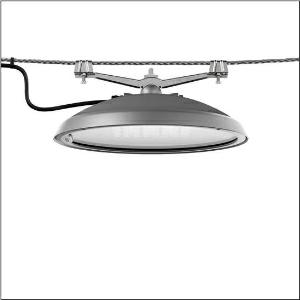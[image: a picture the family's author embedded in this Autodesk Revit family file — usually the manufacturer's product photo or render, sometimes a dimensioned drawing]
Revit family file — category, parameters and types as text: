
# Revit family: dl_50_iq_mini___p1_0s_5xa248u31f08ge_bd95
name_source: partatom
category: Lighting Fixtures
units: mm (PartAtom-declared; Revit-internal decimal feet)

## family parameters
Cut with Voids When Loaded = No
Host = Face
Light Source = No
Part Type = Normal
Room Calculation Point = No
Round Connector Dimension = Use Diameter
Shared = No

## types (1)
- --- (1 x LED, 5030 lm, 32.7 W, 3000K)
    Apparent Load = 33 VA
    CIE Flux Codes = 23 54 93 100 100
    Color Rendering = 70
    Color Temperature = 3000K
    Default Elevation = 1800 mm
    Description = DL 50 iQ mini, catenary luminaire, primary light control with lens, of PMMA, primary optical cover: cover, of toughened safety glass, transparent, light distribution: P1.0s, light emission: direct distribution, primary light characteristic: symmetric, installation type: suspended mounting, LED, High Power LED, rated luminous flux: 5.030lm, luminous efficacy: 154lm/W, light colour: 730, colour temperature: 3000K, control gear: iQ Street-Remote, control: optimised constant luminous flux control (CLO 2.0), Desk-Remote (wireless, voltage-free reading and setting of iQ features in the workshop via application-optimized NFC function/RFID function), Light-Fading, Smart-Wire, Night-Set, Lumen-Switch, Temp-Guard, Auto-Match, Street-Remote, mains connection: 230..240V, AC, 50/60Hz, start of lifetime: 33W, end of service life: 34W, reduction: 16W, luminaire housing, of diecast aluminium, powder-coated, SITECO metallic grey (DB 702S), diameter: 500mm, height: 115mm, mounting height: 4..12m, protection rating (complete): IP66, insulation class (complete): insulation class II (safety insulation), certification: CE, ENEC, ENEC+, VDE, impact resistance: IK08, permissible operating ambient temperature for outdoor applications: -25..+40°C, standard-compliant lighting for roads and squares, packaging unit: 1 piece

Light Distribution: P1.0s
    Height = 124 mm
    Lamp = 1 x LED
    Lamp Light Flux = 5030 lm
    Lamp Power = 32.7 W
    Lamp count = 1
    Length = 500 mm
    Luminous efficacy = 154 lm/W
    Manufacturer = Siteco
    ModVariant = No
    Model = 5XA248U31F08GE
    Number of Poles = 1
    OnlyDefault = Yes
    Power Factor = 1
    Product Name = DL 50 iQ mini | P1.0s
    Product group = catenary luminaire
    ProductGroupID = 6300
    Protection Class = Protection class II
    Protection Degree = IP 66
    RLX_Detail_Level = 1
    RLX_Emergency_Light_Flux = 0 lm
    RLX_Emergency_Type = 0
    RLX_Emergency_Type_DB = No
    RlxData = <blob elided: 123485 chars, md5=bc701b0e>
    Socket = socket
    Standby Power = 0 W
    System Light Flux = 5030 lm
    System Power = 33 W
    Type Comments = factory setting: luminous flux: 100 % | dim-lin: 254 | 340 mA
    Type Image = l_1242791.jpg
    URL = http://relux.com
    VarID = @adj_141273
    Voltage = 0 V
    Weight = 0.00 kg
    Width = 0 mm  [stored 0 ft]

note: [stored X ft] marks values corroborated as IEEE doubles in the binary element streams (Revit-internal decimal feet)

## geometry (parser evidence)
native form markers: Blend x4, Sweep x12
no freeform markers — native parametric forms only
